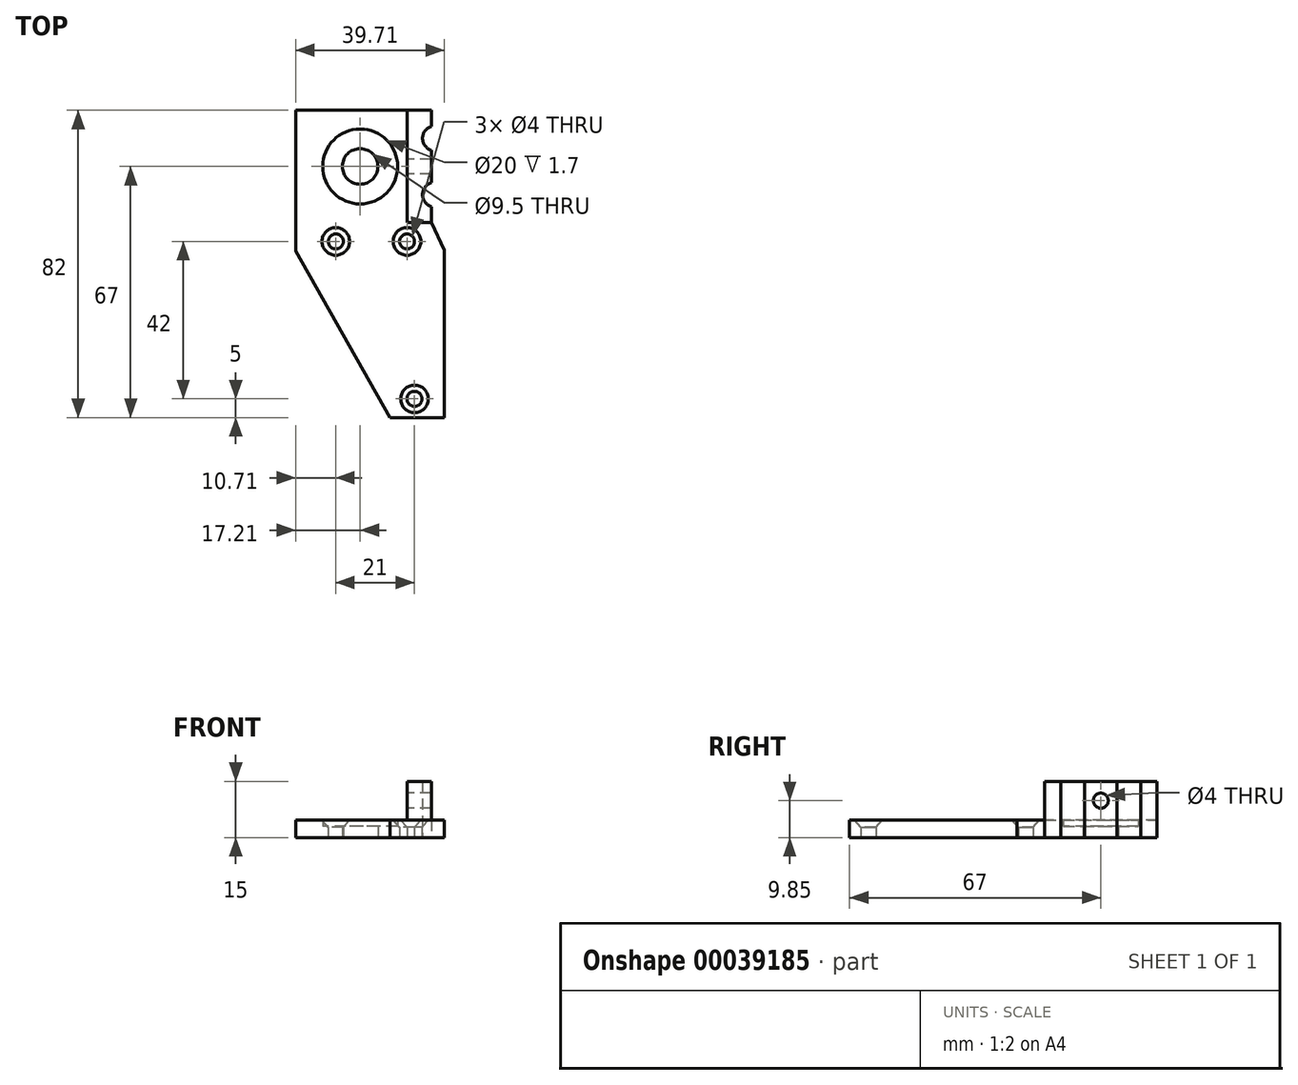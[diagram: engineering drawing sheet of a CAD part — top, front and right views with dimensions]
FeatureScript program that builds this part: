
annotation { "Feature Type Name" : "Feature", "Feature Type Description" : "" }
export const myFeature = defineFeature(function(context is Context, id is Id, definition is map)
    precondition{}
    {
        {
            var Q0;
            Q0=qCreatedBy(makeId("Top.planeOp"),FACE);
            var sketch = newSketch(context, id + "F0", { "sketchPlane" : qUnion([Q0])});
            skLineSegment(sketch, "E0", {"start": v(-52.55, 21) * mm, "end": v(60.16, 21) * mm, "construction": true});
            skLineSegment(sketch, "E1", {"start": v(-53.87, 0) * mm, "end": v(61.05, 0) * mm, "construction": true});
            skLineSegment(sketch, "E2.MirrorCS", {"start": v(-52.55, -21) * mm, "end": v(60.16, -21) * mm, "construction": true});
            skCircle(sketch, "E3", {"center": v(-28.55, 21) * mm, "radius": 2 * mm});
            skCircle(sketch, "E4", {"center": v(-9.55, 21) * mm, "radius": 2 * mm});
            skCircle(sketch, "E5", {"center": v(-7.55, -21) * mm, "radius": 2 * mm});
            skLineSegment(sketch, "E6.top", {"start": v(-14.07, -26) * mm, "end": v(0.45, -26) * mm});
            skCircle(sketch, "E7", {"center": v(-28.55, 21) * mm, "radius": 3.5 * mm});
            skCircle(sketch, "E8", {"center": v(-9.55, 21) * mm, "radius": 3.5 * mm});
            skCircle(sketch, "E9", {"center": v(-7.55, -21) * mm, "radius": 3.5 * mm});
            skLineSegment(sketch, "E10", {"start": v(0.45, 18.62) * mm, "end": v(0.45, -26) * mm});
            skLineSegment(sketch, "E11.direction1", {"start": v(0.45, 16) * mm, "end": v(-9.55, 16) * mm, "construction": true});
            skLineSegment(sketch, "E11.direction2", {"start": v(0.45, 16) * mm, "end": v(0.45, 6) * mm, "construction": true});
            skLineSegment(sketch, "E12", {"start": v(-39.26, 18.44) * mm, "end": v(-14.07, -26) * mm});
            skLineSegment(sketch, "E13", {"start": v(-9.55, 56) * mm, "end": v(-9.55, 26) * mm});
            skLineSegment(sketch, "E14", {"start": v(-3.03, 26) * mm, "end": v(-9.55, 26) * mm});
            skLineSegment(sketch, "E15", {"start": v(-9.55, 56) * mm, "end": v(-3.03, 56) * mm});
            skLineSegment(sketch, "E16", {"start": v(-2.05, 56) * mm, "end": v(-2.05, 26.73) * mm, "construction": true});
            skPoint(sketch, "E16.endSnap0", {"position": v(-2.05, 26) * mm});
            skLineSegment(sketch, "E17", {"start": v(5.45, 41) * mm, "end": v(-24.4, 41) * mm, "construction": true});
            skArc(sketch, "E18", {"start": v(-3.03, 51.7) * mm, "mid": v(-5.4, 48.5) * mm, "end": v(-3.03, 45.3) * mm});
            skArc(sketch, "E19.MirrorC", {"start": v(-3.03, 30.3) * mm, "mid": v(-5.4, 33.5) * mm, "end": v(-3.03, 36.7) * mm});
            skLineSegment(sketch, "E20", {"start": v(-3.03, 56) * mm, "end": v(-3.03, 51.7) * mm});
            skLineSegment(sketch, "E21.trimOffspring", {"start": v(-3.03, 45.3) * mm, "end": v(-3.03, 36.7) * mm});
            skLineSegment(sketch, "E22.trimOffspring", {"start": v(-3.03, 30.3) * mm, "end": v(-3.03, 26) * mm});
            skLineSegment(sketch, "E23", {"start": v(-3.03, 26) * mm, "end": v(0.45, 18.62) * mm});
            skPoint(sketch, "E24.orphan", {"position": v(-9.55, 41) * mm});
            skLineSegment(sketch, "E25", {"start": v(-22.05, 56.62) * mm, "end": v(-22.05, 27.41) * mm, "construction": true});
            skCircle(sketch, "E26", {"center": v(-22.05, 41) * mm, "radius": 4.75 * mm});
            skCircle(sketch, "E27", {"center": v(-22.05, 41) * mm, "radius": 10 * mm});
            skLineSegment(sketch, "E28", {"start": v(-9.55, 56) * mm, "end": v(-39.26, 56) * mm});
            skLineSegment(sketch, "E29", {"start": v(-39.26, 56) * mm, "end": v(-39.26, 18.44) * mm});
            skSolve(sketch);
        }
        {
            var Q0;
            Q0=makeQuery(id+"F0.imprint","IMPRINT",FACE,{"disambiguationData":[TD([[makeQuery(id+"F0.imprint","IMPRINT",EDGE,{"derivedFrom":sQuery(id+"F0.wireOp",EDGE,"E6.bottom")}),-1.0]])]});
            var Q1;
            Q1=makeQuery(id+"F0.imprint","IMPRINT",FACE,{"disambiguationData":[TD([[makeQuery(id+"F0.imprint","IMPRINT",EDGE,{"derivedFrom":sQuery(id+"F0.wireOp",EDGE,"E3")}),-1.0]])]});
            var Q2;
            Q2=makeQuery(id+"F0.imprint","IMPRINT",FACE,{"disambiguationData":[TD([[makeQuery(id+"F0.imprint","IMPRINT",EDGE,{"derivedFrom":sQuery(id+"F0.wireOp",EDGE,"E4")}),-1.0]])]});
            var Q3;
            Q3=makeQuery(id+"F0.imprint","IMPRINT",FACE,{"disambiguationData":[TD([[makeQuery(id+"F0.imprint","IMPRINT",EDGE,{"derivedFrom":sQuery(id+"F0.wireOp",EDGE,"E5")}),-1.0]])]});
            var Q4;
            Q4=makeQuery(id+"F0.imprint","IMPRINT",FACE,{"disambiguationData":[TD([[makeQuery(id+"F0.imprint","IMPRINT",EDGE,{"derivedFrom":sQuery(id+"F0.wireOp",EDGE,"E6.top")}),1.0]])]});
            var Q5;
            Q5=makeQuery(id+"F0.imprint","IMPRINT",FACE,{"disambiguationData":[TD([[makeQuery(id+"F0.imprint","IMPRINT",EDGE,{"derivedFrom":sQuery(id+"F0.wireOp",EDGE,"E13")}),1.0]])]});
            extrude(context, id + "F1", {"entities" : qUnion([Q0, Q1, Q2, Q3, Q4, Q5]), "depth" : 4.7 * mm});
        }
        {
            var Q0;
            Q0=makeQuery(id+"F1.opExtrude","CAP_EDGE",EDGE,{"disambiguationData":[OSD([sQuery(id+"F0.wireOp",EDGE,"E3")])],"isStart":false});
            var Q1;
            Q1=makeQuery(id+"F1.opExtrude","CAP_EDGE",EDGE,{"disambiguationData":[OSD([sQuery(id+"F0.wireOp",EDGE,"E4")])],"isStart":false});
            var Q2;
            Q2=makeQuery(id+"F1.opExtrude","CAP_EDGE",EDGE,{"disambiguationData":[OSD([sQuery(id+"F0.wireOp",EDGE,"E5")])],"isStart":false});
            chamfer(context, id + "F2", {"entities" : qUnion([Q0, Q1, Q2]), "chamferType" : ChamferType.OFFSET_ANGLE, "width" : 2 * mm, "oppositeDirection" : false, "angle" : 40 * degree, "tangentPropagation" : true});
        }
        {
            var Q0;
            Q0=makeQuery(id+"F0.imprint","IMPRINT",FACE,{"disambiguationData":[TD([[makeQuery(id+"F0.imprint","IMPRINT",EDGE,{"derivedFrom":sQuery(id+"F0.wireOp",EDGE,"E13")}),1.0]])]});
            extrude(context, id + "F3", {"entities" : qUnion([Q0]), "operationType" : NewBodyOperationType.ADD, "depth" : 15 * mm});
        }
        {
            var Q0;
            Q0=makeQuery(id+"F0.imprint","IMPRINT",FACE,{"disambiguationData":[TD([[makeQuery(id+"F0.imprint","IMPRINT",EDGE,{"derivedFrom":sQuery(id+"F0.wireOp",EDGE,"E26")}),-1.0]])]});
            extrude(context, id + "F4", {"entities" : qUnion([Q0]), "operationType" : NewBodyOperationType.ADD, "depth" : 3 * mm});
        }
        {
            var Q0;
            Q0=makeQuery(id+"F3.opExtrude","SWEPT_FACE",FACE,{"disambiguationData":[OSD([sQuery(id+"F0.wireOp",EDGE,"E13")])]});
            var sketch = newSketch(context, id + "F5", { "sketchPlane" : qUnion([Q0])});
            skLineSegment(sketch, "E30", {"start": v(-55.55, 9.85) * mm, "end": v(-26.6, 9.85) * mm, "construction": true});
            skPoint(sketch, "E30.startSnap0", {"position": v(-56, 9.85) * mm});
            skLineSegment(sketch, "E31", {"start": v(-41, 15) * mm, "end": v(-41, 5.45) * mm, "construction": true});
            skCircle(sketch, "E32", {"center": v(-41, 9.85) * mm, "radius": 2 * mm});
            skSolve(sketch);
        }
        {
            var Q0;
            Q0=makeQuery(id+"F5.imprint","IMPRINT",FACE,{"disambiguationData":[TD([[makeQuery(id+"F5.imprint","IMPRINT",EDGE,{"derivedFrom":sQuery(id+"F5.wireOp",EDGE,"E32")}),1.0]])]});
            extrude(context, id + "F6", {"entities" : qUnion([Q0]), "operationType" : NewBodyOperationType.REMOVE, "oppositeDirection" : true, "depth" : 8 * mm});
        }
    });
